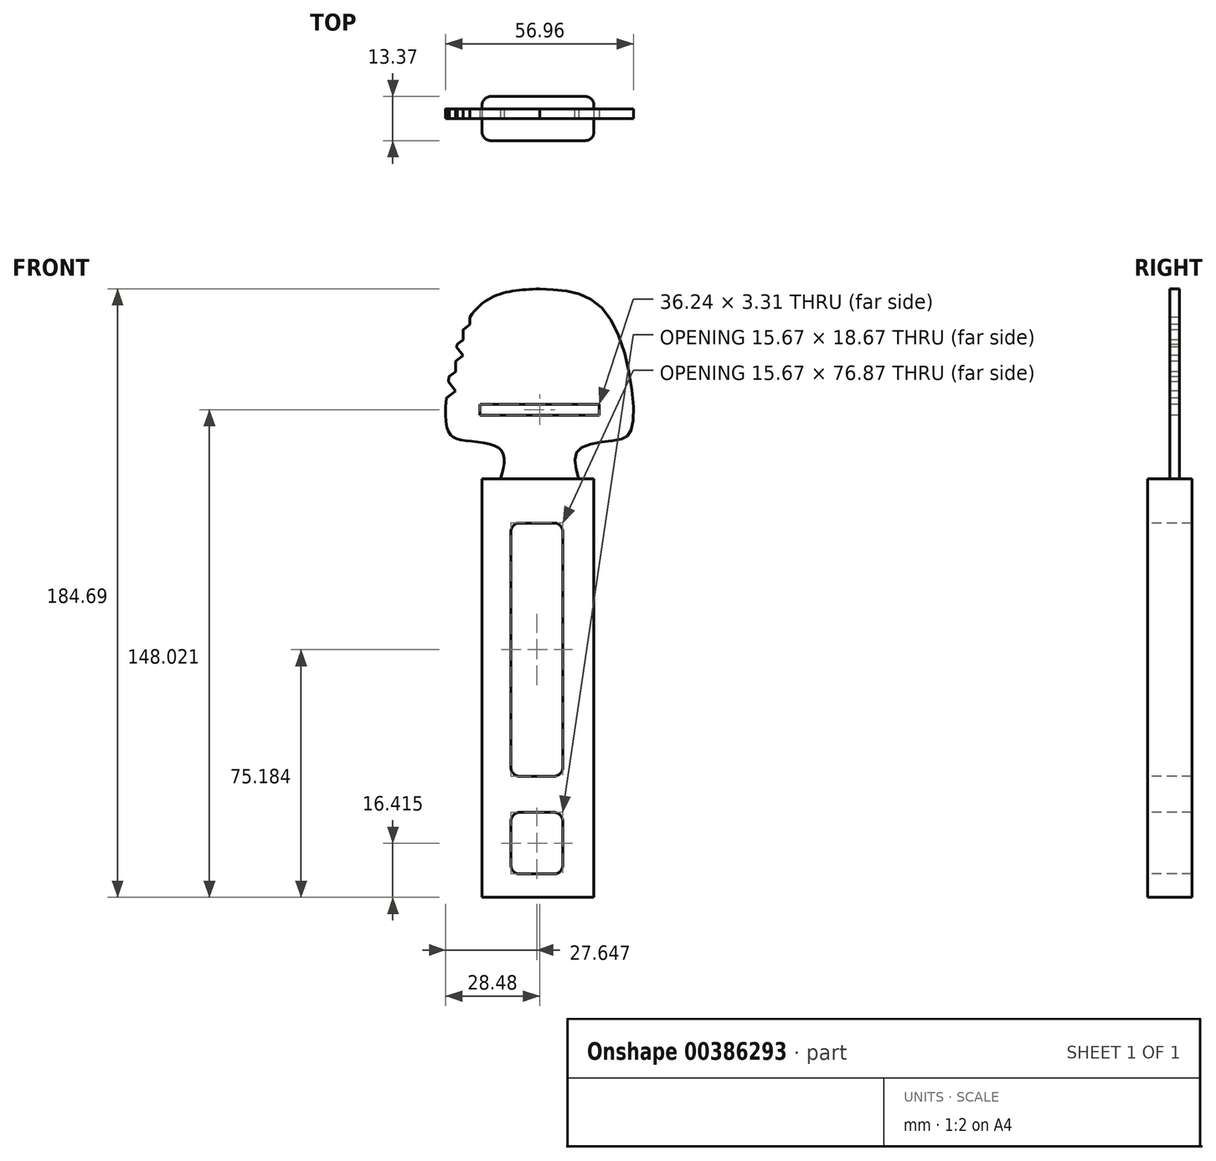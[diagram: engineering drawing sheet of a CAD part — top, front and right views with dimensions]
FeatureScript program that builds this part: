
annotation { "Feature Type Name" : "Feature", "Feature Type Description" : "" }
export const myFeature = defineFeature(function(context is Context, id is Id, definition is map)
    precondition{}
    {
        {
            var Q0;
            Q0=qCreatedBy(makeId("Top.planeOp"),FACE);
            var sketch = newSketch(context, id + "F0", { "sketchPlane" : qUnion([Q0])});
            skLineSegment(sketch, "E0.bottom", {"start": v(-14.87, 3.72) * mm, "end": v(13.93, 3.72) * mm});
            skLineSegment(sketch, "E0.top", {"start": v(-14.87, -9.65) * mm, "end": v(13.93, -9.65) * mm});
            skLineSegment(sketch, "E0.left", {"start": v(-17.41, 1.18) * mm, "end": v(-17.41, -7.1) * mm});
            skLineSegment(sketch, "E0.right", {"start": v(16.47, 1.18) * mm, "end": v(16.47, -7.1) * mm});
            skPoint(sketch, "E1.visualSharp", {"position": v(-17.41, 3.72) * mm});
            skArc(sketch, "E1.filletArc", {"start": v(-14.87, 3.72) * mm, "mid": v(-16.67, 2.98) * mm, "end": v(-17.41, 1.18) * mm});
            skPoint(sketch, "E2.visualSharp", {"position": v(16.47, 3.72) * mm});
            skArc(sketch, "E2.filletArc", {"start": v(16.47, 1.18) * mm, "mid": v(15.73, 2.98) * mm, "end": v(13.93, 3.72) * mm});
            skPoint(sketch, "E3.visualSharp", {"position": v(16.47, -9.65) * mm});
            skArc(sketch, "E3.filletArc", {"start": v(13.93, -9.65) * mm, "mid": v(15.73, -8.9) * mm, "end": v(16.47, -7.1) * mm});
            skPoint(sketch, "E4.visualSharp", {"position": v(-17.41, -9.65) * mm});
            skArc(sketch, "E4.filletArc", {"start": v(-17.41, -7.1) * mm, "mid": v(-16.67, -8.9) * mm, "end": v(-14.87, -9.65) * mm});
            skSolve(sketch);
        }
        {
            var Q0;
            Q0=makeQuery(id+"F0.imprint","IMPRINT",FACE,{"disambiguationData":[TD([[makeQuery(id+"F0.imprint","IMPRINT",EDGE,{"derivedFrom":sQuery(id+"F0.wireOp",EDGE,"E0.bottom")}),-1.0]])]});
            extrude(context, id + "F1", {"entities" : qUnion([Q0]), "depth" : 127 * mm});
        }
        {
            var Q0;
            Q0=makeQuery(id+"F1.opExtrude","SWEPT_FACE",FACE,{"disambiguationData":[OSD([sQuery(id+"F0.wireOp",EDGE,"E0.top")])]});
            cPlane(context, id + "F2", {"entities" : qUnion([Q0]), "cplaneType" : CPlaneType.OFFSET, "offset" : 0 * mm, "width" : 152.4 * mm, "height" : 152.4 * mm});
        }
        {
            var Q0;
            Q0=qCreatedBy(id+"F2.planeOp",FACE);
            var sketch = newSketch(context, id + "F3", { "sketchPlane" : qUnion([Q0])});
            skLineSegment(sketch, "E5.bottom", {"start": v(-6.13, 113.62) * mm, "end": v(4.46, 113.62) * mm});
            skLineSegment(sketch, "E5.top", {"start": v(-6.13, 36.75) * mm, "end": v(4.46, 36.75) * mm});
            skLineSegment(sketch, "E5.left", {"start": v(-8.67, 111.08) * mm, "end": v(-8.67, 39.3) * mm});
            skLineSegment(sketch, "E5.right", {"start": v(7, 111.08) * mm, "end": v(7, 39.3) * mm});
            skLineSegment(sketch, "E6.bottom", {"start": v(-6.13, 25.75) * mm, "end": v(4.46, 25.75) * mm});
            skLineSegment(sketch, "E6.top", {"start": v(-6.13, 7.08) * mm, "end": v(4.46, 7.08) * mm});
            skLineSegment(sketch, "E6.left", {"start": v(-8.67, 23.2) * mm, "end": v(-8.67, 9.62) * mm});
            skLineSegment(sketch, "E6.right", {"start": v(7, 23.2) * mm, "end": v(7, 9.62) * mm});
            skPoint(sketch, "E7.visualSharp", {"position": v(-8.67, 113.62) * mm});
            skArc(sketch, "E7.filletArc", {"start": v(-6.13, 113.62) * mm, "mid": v(-7.92, 112.87) * mm, "end": v(-8.67, 111.08) * mm});
            skPoint(sketch, "E8.visualSharp", {"position": v(7, 113.62) * mm});
            skArc(sketch, "E8.filletArc", {"start": v(7, 111.08) * mm, "mid": v(6.26, 112.87) * mm, "end": v(4.46, 113.62) * mm});
            skPoint(sketch, "E9.visualSharp", {"position": v(7, 36.75) * mm});
            skArc(sketch, "E9.filletArc", {"start": v(4.46, 36.75) * mm, "mid": v(6.26, 37.5) * mm, "end": v(7, 39.3) * mm});
            skPoint(sketch, "E10.visualSharp", {"position": v(-8.67, 36.75) * mm});
            skArc(sketch, "E10.filletArc", {"start": v(-8.67, 39.3) * mm, "mid": v(-7.92, 37.5) * mm, "end": v(-6.13, 36.75) * mm});
            skPoint(sketch, "E11.visualSharp", {"position": v(-8.67, 25.75) * mm});
            skArc(sketch, "E11.filletArc", {"start": v(-6.13, 25.75) * mm, "mid": v(-7.92, 25) * mm, "end": v(-8.67, 23.2) * mm});
            skPoint(sketch, "E12.visualSharp", {"position": v(-8.67, 7.08) * mm});
            skArc(sketch, "E12.filletArc", {"start": v(-8.67, 9.62) * mm, "mid": v(-7.92, 7.82) * mm, "end": v(-6.13, 7.08) * mm});
            skPoint(sketch, "E13.visualSharp", {"position": v(7, 7.08) * mm});
            skArc(sketch, "E13.filletArc", {"start": v(4.46, 7.08) * mm, "mid": v(6.26, 7.82) * mm, "end": v(7, 9.62) * mm});
            skPoint(sketch, "E14.visualSharp", {"position": v(7, 25.75) * mm});
            skArc(sketch, "E14.filletArc", {"start": v(7, 23.2) * mm, "mid": v(6.26, 25) * mm, "end": v(4.46, 25.75) * mm});
            skSolve(sketch);
        }
        {
            var Q0;
            Q0=makeQuery(id+"F3.imprint","IMPRINT",FACE,{"disambiguationData":[TD([[makeQuery(id+"F3.imprint","IMPRINT",EDGE,{"derivedFrom":sQuery(id+"F3.wireOp",EDGE,"E5.bottom")}),-1.0]])]});
            var Q1;
            Q1=makeQuery(id+"F3.imprint","IMPRINT",FACE,{"disambiguationData":[TD([[makeQuery(id+"F3.imprint","IMPRINT",EDGE,{"derivedFrom":sQuery(id+"F3.wireOp",EDGE,"E6.bottom")}),-1.0]])]});
            extrude(context, id + "F4", {"entities" : qUnion([Q0, Q1]), "operationType" : NewBodyOperationType.REMOVE, "oppositeDirection" : true, "depth" : 25.4 * mm});
        }
        {
            var Q0;
            Q0=makeQuery(id+"F1.opExtrude","CAP_FACE",FACE,{"disambiguationData":[OSD([sQuery(id+"F0.wireOp",EDGE,"E0.bottom"),sQuery(id+"F0.wireOp",EDGE,"E0.top"),sQuery(id+"F0.wireOp",EDGE,"E0.left"),sQuery(id+"F0.wireOp",EDGE,"E0.right"),sQuery(id+"F0.wireOp",EDGE,"E1.filletArc"),sQuery(id+"F0.wireOp",EDGE,"E2.filletArc"),sQuery(id+"F0.wireOp",EDGE,"E3.filletArc"),sQuery(id+"F0.wireOp",EDGE,"E4.filletArc")])],"isStart":false});
            var sketch = newSketch(context, id + "F5", { "sketchPlane" : qUnion([Q0])});
            skPoint(sketch, "E15.oppositeSnap0", {"position": v(16.47, -2.96) * mm});
            skLineSegment(sketch, "E15.bottom", {"start": v(-31.06, 0) * mm, "end": v(29.89, 0) * mm});
            skLineSegment(sketch, "E15.top", {"start": v(-31.06, -2.96) * mm, "end": v(29.89, -2.96) * mm});
            skLineSegment(sketch, "E15.left", {"start": v(-31.06, 0) * mm, "end": v(-31.06, -2.96) * mm});
            skLineSegment(sketch, "E15.right", {"start": v(29.89, 0) * mm, "end": v(29.89, -2.96) * mm});
            skSolve(sketch);
        }
        {
            var Q0;
            {var subQ0=sQuery(id+"F5.wireOp",EDGE,"E15.left");Q0=makeQuery(id+"F5.imprint","IMPRINT",FACE,{"disambiguationData":[TD([[makeQuery(id+"F5.imprint","IMPRINT",EDGE,{"derivedFrom":subQ0}),1.0]])]});}
            var Q1;
            {var subQ0=sQuery(id+"F5.wireOp",EDGE,"E15.bottom");var subQ1=makeQuery(id+"F1.opExtrude","CAP_EDGE",EDGE,{"disambiguationData":[OSD([sQuery(id+"F0.wireOp",EDGE,"E0.left")])],"isStart":false});var subQ2=makeQuery(id+"F5.imprint","INTERSECT",VERTEX,{"derivedFrom":[subQ1,subQ0]});Q1=makeQuery(id+"F5.imprint","IMPRINT",FACE,{"disambiguationData":[TD([[makeQuery(id+"F5.imprint","IMPRINT",EDGE,{"disambiguationData":[TD([[subQ2,-1.0]])],"derivedFrom":subQ0}),-1.0]])]});}
            var Q2;
            {var subQ0=sQuery(id+"F5.wireOp",EDGE,"E15.right");Q2=makeQuery(id+"F5.imprint","IMPRINT",FACE,{"disambiguationData":[TD([[makeQuery(id+"F5.imprint","IMPRINT",EDGE,{"derivedFrom":subQ0}),-1.0]])]});}
            extrude(context, id + "F6", {"entities" : qUnion([Q0, Q1, Q2]), "operationType" : NewBodyOperationType.ADD, "depth" : 63.5 * mm});
        }
        {
            var Q0;
            Q0=qCreatedBy(id+"F2.planeOp",FACE);
            var sketch = newSketch(context, id + "F7", { "sketchPlane" : qUnion([Q0])});
            skLineSegment(sketch, "E16", {"start": v(0, 108.92) * mm, "end": v(0, 192.07) * mm, "construction": true});
            skSolve(sketch);
        }
        {
            var Q0;
            Q0=makeQuery(id+"F6.opExtrude","SWEPT_FACE",FACE,{"disambiguationData":[OSD([sQuery(id+"F5.wireOp",EDGE,"E15.top")])]});
            var sketch = newSketch(context, id + "F8", { "sketchPlane" : qUnion([Q0])});
            skFitSpline(sketch, "E17", {"points": [v(-11.84, 127) * mm, v(-11.84, 135.9) * mm, v(-24, 138.9) * mm, v(-28.2, 143.26) * mm, v(-20.1, 177.48) * mm, v(0, 184.69) * mm], "startDerivative": vector(18.76, 68.81) * mm, "endDerivative": vector(94.84, 4) * mm});
            skFitSpline(sketch, "E18.MirrorCS", {"points": [v(11.84, 127) * mm, v(11.84, 135.9) * mm, v(24, 138.9) * mm, v(28.2, 143.26) * mm, v(20.1, 177.48) * mm, v(0, 184.69) * mm], "startDerivative": vector(-18.76, 68.81) * mm, "endDerivative": vector(-94.84, 4) * mm});
            skSolve(sketch);
        }
        {
            var Q0;
            {var subQ4=sQuery(id+"F8.wireOp",EDGE,"E17");Q0=makeQuery(id+"F8.imprint","IMPRINT",FACE,{"disambiguationData":[TD([[makeQuery(id+"F8.imprint","IMPRINT",EDGE,{"derivedFrom":subQ4}),1.0]])]});}
            extrude(context, id + "F9", {"entities" : qUnion([Q0]), "operationType" : NewBodyOperationType.REMOVE, "oppositeDirection" : true, "depth" : 25.4 * mm});
        }
        {
            var Q0;
            Q0=makeQuery(id+"F6.opExtrude","SWEPT_FACE",FACE,{"disambiguationData":[OSD([sQuery(id+"F5.wireOp",EDGE,"E15.top")])]});
            cPlane(context, id + "F10", {"entities" : qUnion([Q0]), "cplaneType" : CPlaneType.OFFSET, "offset" : 25.4 * mm, "width" : 152.4 * mm, "height" : 152.4 * mm});
        }
        {
            var Q0;
            Q0=qCreatedBy(id+"F10.planeOp",FACE);
            var sketch = newSketch(context, id + "F11", { "sketchPlane" : qUnion([Q0])});
            skLineSegment(sketch, "E19", {"start": v(0, 149.68) * mm, "end": v(-18.12, 149.68) * mm});
            skLineSegment(sketch, "E20", {"start": v(-18.12, 149.68) * mm, "end": v(-18.12, 146.37) * mm});
            skLineSegment(sketch, "E21", {"start": v(-18.12, 146.37) * mm, "end": v(0, 146.37) * mm});
            skPoint(sketch, "E22.MirrorCS.end.orphan", {"position": v(-18.12, 152.98) * mm});
            skPoint(sketch, "E22.MirrorCS.start.orphan", {"position": v(-18.12, 149.68) * mm});
            skPoint(sketch, "E23.MirrorCS.end.orphan", {"position": v(0, 152.98) * mm});
            skLineSegment(sketch, "E24.MirrorCS", {"start": v(18.12, 149.68) * mm, "end": v(18.12, 146.37) * mm});
            skLineSegment(sketch, "E25.MirrorCS", {"start": v(0, 149.68) * mm, "end": v(18.12, 149.68) * mm});
            skLineSegment(sketch, "E26.MirrorCS", {"start": v(18.12, 146.37) * mm, "end": v(0, 146.37) * mm});
            skSolve(sketch);
        }
        {
            var Q0;
            Q0=makeQuery(id+"F11.imprint","IMPRINT",FACE,{"disambiguationData":[TD([[makeQuery(id+"F11.imprint","IMPRINT",EDGE,{"derivedFrom":sQuery(id+"F11.wireOp",EDGE,"E19")}),1.0]])]});
            extrude(context, id + "F12", {"entities" : qUnion([Q0]), "operationType" : NewBodyOperationType.REMOVE, "oppositeDirection" : true, "depth" : 25.4 * mm});
        }
        {
            var Q0;
            Q0 = qSketchRegion(id + "F11", true);
            extrude(context, id + "F13", {"entities" : qUnion([Q0]), "operationType" : NewBodyOperationType.REMOVE, "oppositeDirection" : true, "depth" : 101.6 * mm});
        }
        {
            var Q0;
            Q0=qCreatedBy(id+"F10.planeOp",FACE);
            var sketch = newSketch(context, id + "F14", { "sketchPlane" : qUnion([Q0])});
            skLineSegment(sketch, "E27", {"start": v(-28.28, 151.54) * mm, "end": v(-25.49, 153.68) * mm});
            skLineSegment(sketch, "E28", {"start": v(-25.49, 153.68) * mm, "end": v(-28.32, 157.39) * mm});
            skLineSegment(sketch, "E29", {"start": v(-28.32, 157.39) * mm, "end": v(-25.49, 159.56) * mm});
            skLineSegment(sketch, "E30", {"start": v(-25.49, 159.56) * mm, "end": v(-25.49, 162.72) * mm});
            skLineSegment(sketch, "E31", {"start": v(-25.49, 162.72) * mm, "end": v(-23.21, 164.46) * mm});
            skLineSegment(sketch, "E32", {"start": v(-23.21, 164.46) * mm, "end": v(-25.49, 167.43) * mm});
            skLineSegment(sketch, "E33", {"start": v(-25.49, 167.43) * mm, "end": v(-23.21, 169.17) * mm});
            skLineSegment(sketch, "E34", {"start": v(-23.21, 169.17) * mm, "end": v(-23.21, 172.25) * mm});
            skLineSegment(sketch, "E35", {"start": v(-23.21, 172.25) * mm, "end": v(-21.14, 173.83) * mm});
            skLineSegment(sketch, "E36", {"start": v(-21.14, 173.83) * mm, "end": v(-21.14, 176.52) * mm});
            skLineSegment(sketch, "E37", {"start": v(-21.14, 176.52) * mm, "end": v(-30.75, 169.17) * mm});
            skLineSegment(sketch, "E38", {"start": v(-30.75, 169.17) * mm, "end": v(-30.75, 151.54) * mm});
            skLineSegment(sketch, "E39", {"start": v(-30.75, 151.54) * mm, "end": v(-28.28, 151.54) * mm});
            skSolve(sketch);
        }
        {
            var Q0;
            Q0=makeQuery(id+"F14.imprint","IMPRINT",FACE,{"disambiguationData":[TD([[makeQuery(id+"F14.imprint","IMPRINT",EDGE,{"derivedFrom":sQuery(id+"F14.wireOp",EDGE,"E27")}),1.0]])]});
            extrude(context, id + "F15", {"entities" : qUnion([Q0]), "operationType" : NewBodyOperationType.REMOVE, "oppositeDirection" : true, "depth" : 101.6 * mm});
        }
    });
